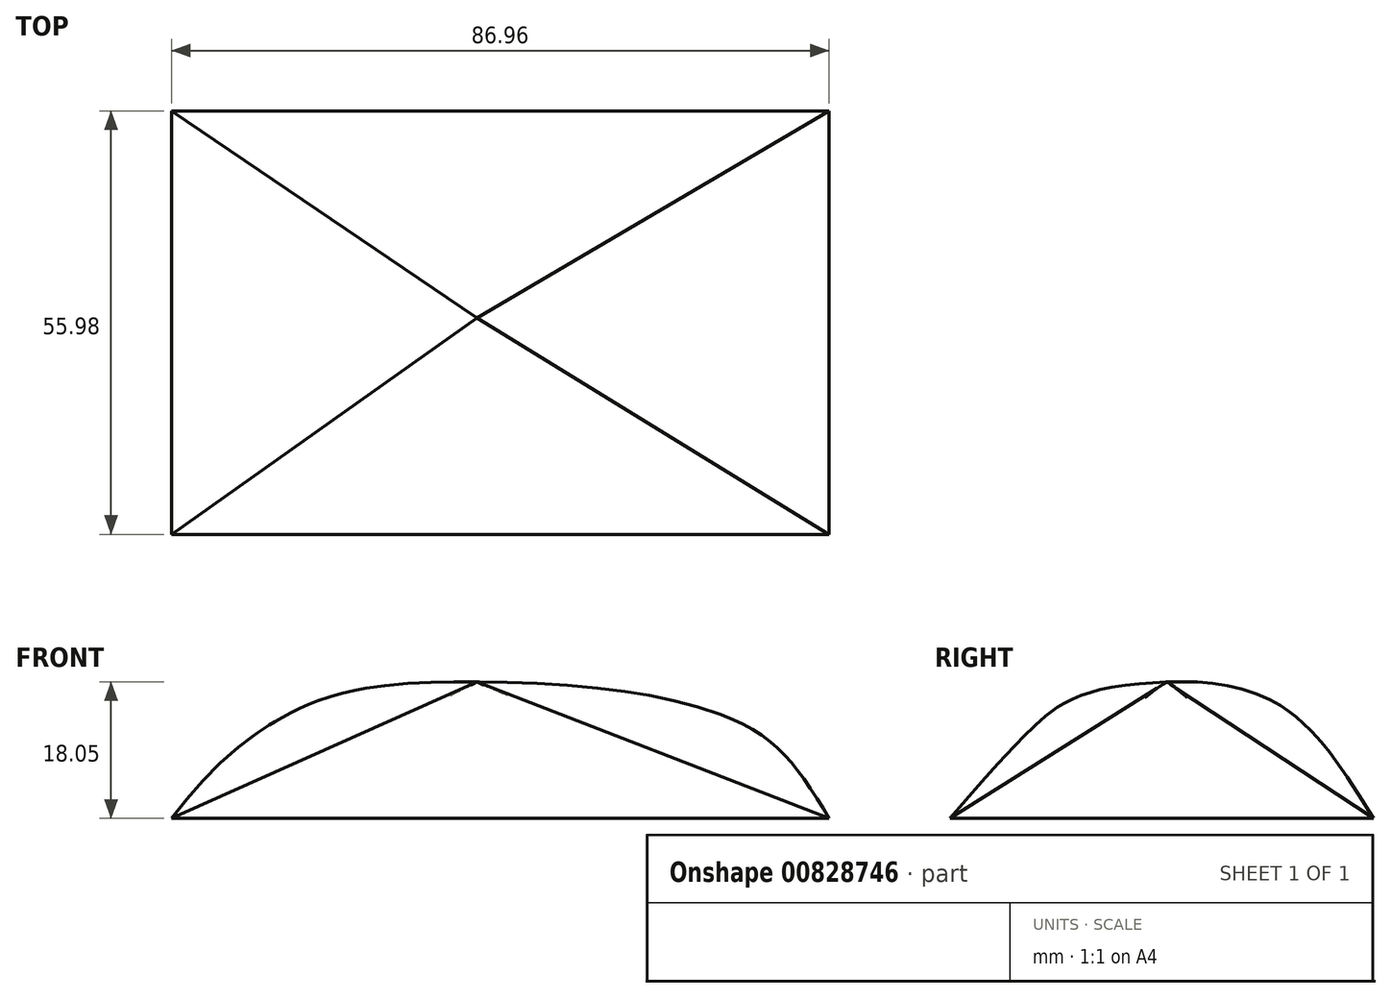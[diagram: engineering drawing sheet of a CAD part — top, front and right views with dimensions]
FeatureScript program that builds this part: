
annotation { "Feature Type Name" : "Feature", "Feature Type Description" : "" }
export const myFeature = defineFeature(function(context is Context, id is Id, definition is map)
    precondition{}
    {
        {
            var Q0;
            Q0=qCreatedBy(makeId("Top.planeOp"),FACE);
            var sketch = newSketch(context, id + "F0", { "sketchPlane" : qUnion([Q0])});
            skLineSegment(sketch, "E0.bottom", {"start": v(-40.4, 27.34) * mm, "end": v(46.56, 27.34) * mm});
            skLineSegment(sketch, "E0.top", {"start": v(-40.4, -28.64) * mm, "end": v(46.56, -28.64) * mm});
            skLineSegment(sketch, "E0.left", {"start": v(-40.4, 27.34) * mm, "end": v(-40.4, -28.64) * mm});
            skLineSegment(sketch, "E0.right", {"start": v(46.56, 27.34) * mm, "end": v(46.56, -28.64) * mm});
            skSolve(sketch);
        }
        {
            var Q0;
            Q0=qCreatedBy(makeId("Front.planeOp"),FACE);
            var sketch = newSketch(context, id + "F1", { "sketchPlane" : qUnion([Q0])});
            skLineSegment(sketch, "E1", {"start": v(0, 0) * mm, "end": v(0, 18) * mm, "construction": true});
            skSolve(sketch);
        }
        {
            var Q0;
            Q0=qCreatedBy(makeId("Right.planeOp"),FACE);
            var sketch = newSketch(context, id + "F2", { "sketchPlane" : qUnion([Q0])});
            skFitSpline(sketch, "E2", {"points": [v(27.34, 0) * mm, v(18.77, 11.9) * mm, v(0, 18) * mm], "startDerivative": vector(-19.5, 30.75) * mm, "endDerivative": vector(-55.59, -2.47) * mm});
            skFitSpline(sketch, "E3", {"points": [v(-28.64, 0) * mm, v(-17.8, 11.89) * mm, v(0, 18) * mm], "startDerivative": vector(24.86, 29.6) * mm, "endDerivative": vector(65.65, 2.64) * mm});
            skSolve(sketch);
        }
        {
            var Q0;
            Q0=qCreatedBy(makeId("Front.planeOp"),FACE);
            var sketch = newSketch(context, id + "F3", { "sketchPlane" : qUnion([Q0])});
            skFitSpline(sketch, "E4", {"points": [v(-40.4, 0) * mm, v(-25.98, 13.2) * mm, v(0, 18) * mm], "startDerivative": vector(35.73, 46.43) * mm, "endDerivative": vector(81.2, -1.62) * mm});
            skFitSpline(sketch, "E5", {"points": [v(46.56, 0) * mm, v(35.18, 12.44) * mm, v(0, 18) * mm], "startDerivative": vector(-28.33, 46.5) * mm, "endDerivative": vector(-73.2, -0.34) * mm});
            skSolve(sketch);
        }
        {
            var Q0;
            Q0=makeQuery(id+"F0.imprint","IMPRINT",FACE,{"disambiguationData":[TD([[makeQuery(id+"F0.imprint","IMPRINT",EDGE,{"derivedFrom":sQuery(id+"F0.wireOp",EDGE,"E0.bottom")}),-1.0]])]});
            var Q1;
            Q1=sQuery(id+"F1.wireOp",VERTEX,"E1.end");
            var Q2;
            Q2=sQuery(id+"F3.wireOp",EDGE,"E5");
            var Q3;
            Q3=sQuery(id+"F2.wireOp",EDGE,"E2");
            var Q4;
            Q4=sQuery(id+"F2.wireOp",EDGE,"E3");
            var Q5;
            Q5=sQuery(id+"F3.wireOp",EDGE,"E4");
            loft(context, id + "F4", {"addGuides" : true, "sheetProfilesArray" : [{ "sheetProfileEntities" : qUnion([Q0]) }, { "sheetProfileEntities" : qUnion([Q1]) }], "guidesArray" : [{ "guideEntities" : qUnion([Q2]), "guideDerivativeType" : LoftGuideDerivativeType.DEFAULT, "guideDerivativeMagnitude" : 1 }, { "guideEntities" : qUnion([Q3]), "guideDerivativeType" : LoftGuideDerivativeType.DEFAULT, "guideDerivativeMagnitude" : 1 }, { "guideEntities" : qUnion([Q4]), "guideDerivativeType" : LoftGuideDerivativeType.DEFAULT, "guideDerivativeMagnitude" : 1 }, { "guideEntities" : qUnion([Q5]), "guideDerivativeType" : LoftGuideDerivativeType.DEFAULT, "guideDerivativeMagnitude" : 1 }]});
        }
    });
